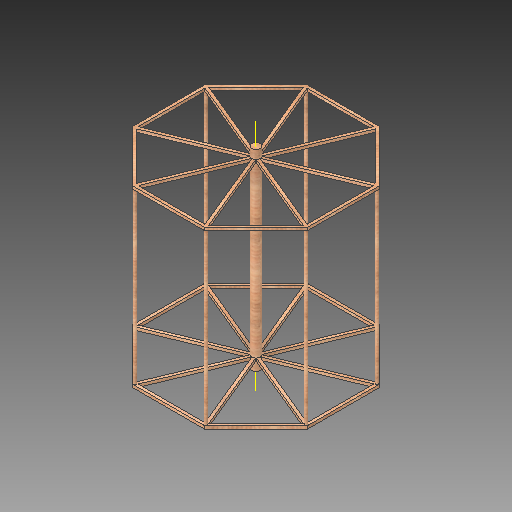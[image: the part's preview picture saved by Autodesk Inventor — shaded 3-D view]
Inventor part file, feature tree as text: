
AUTODESK INVENTOR PART (.ipt)
format: ipt  version: 2019 (Build 230136000, 136)  size: 355,328 bytes
history: native  units: mm
features: sketch x6, extrude x5, plane x2, mirror x2, pattern_circular x2, projected_geometry x2, shell x1, other x1
ambient origin geometry x8: Origin, YZ Plane, XZ Plane, XY Plane, X Axis, Y Axis, Z Axis, Center Point
bodies: Solid1 (feature_tree)
feature tree (21):
  sketch  "Sketch1"  dims[d0=600.0mm d1=10.0mm d2=0.0mm d11=10.0mm]
  extrude  "Extrusion1"  Depth=10.0mm TaperAngle=0.0deg
  sketch  "Sketch2"  dims[d12=29.5mm d13=30.0mm d14=630.0mm d15=0.0mm d16=0.0mm]
  plane  "Work Plane1"
  mirror  "Mirror1"
  sketch  "Sketch6"  dims[d17=10.0mm d18=10.0mm]
  shell  "Shell3"  Thickness=10.0mm
  extrude  "Extrusion3"  Depth=30.0mm TaperAngle=0.0deg
  plane  "Work Plane3"
  sketch  "Sketch8"  dims[d26=10.0mm d27=580.0mm d28=0.0mm d29=80.0mm d30=360.0deg]
  extrude  "Extrusion4"  Depth=10.0mm
  extrude  "Extrusion5"  Depth=30.0mm TaperAngle=0.0deg
  other  "Work Axis1"
  pattern_circular  "Circular Pattern1"  Count=8 Angle=360.0deg
  mirror  "Mirror2"
  extrude  "Extrusion6"  Depth=580.0mm TaperAngle=0.0deg
  pattern_circular  "Circular Pattern2"  Count=8 Angle=360.0deg
  sketch  "Sketch7"  dims[d19=30.0mm d20=0.0mm d21=30.0mm d22=0.0mm d23=80.0mm d24=360.0deg]
  sketch  "Sketch9"
  projected_geometry  "Projected Loop1"
  projected_geometry  "Projected Loop2"
